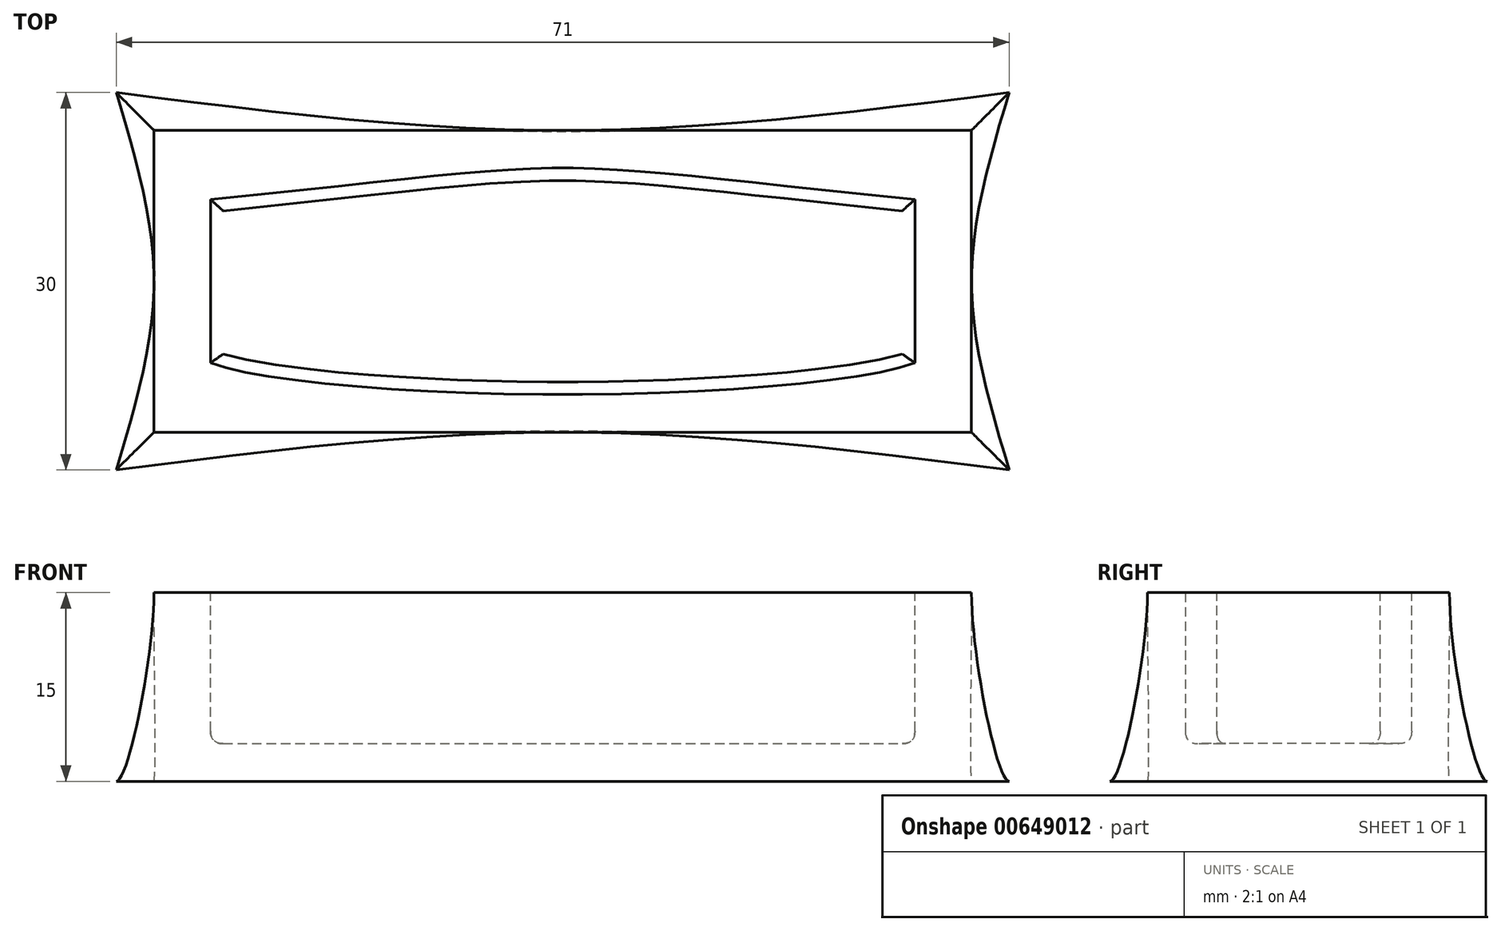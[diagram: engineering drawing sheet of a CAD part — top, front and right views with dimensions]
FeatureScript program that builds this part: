
annotation { "Feature Type Name" : "Feature", "Feature Type Description" : "" }
export const myFeature = defineFeature(function(context is Context, id is Id, definition is map)
    precondition{}
    {
        {
            var Q0;
            Q0=qCreatedBy(makeId("Top.planeOp"),FACE);
            var sketch = newSketch(context, id + "F0", { "sketchPlane" : qUnion([Q0])});
            skLineSegment(sketch, "E0", {"start": v(-35.5, 0) * mm, "end": v(35.5, 0) * mm, "construction": true});
            skLineSegment(sketch, "E1", {"start": v(-35.5, 0) * mm, "end": v(-35.5, 15) * mm, "construction": true});
            skLineSegment(sketch, "E2", {"start": v(35.5, 0) * mm, "end": v(35.5, 15) * mm, "construction": true});
            skLineSegment(sketch, "E3", {"start": v(0, 0) * mm, "end": v(0, 12) * mm, "construction": true});
            skLineSegment(sketch, "E4", {"start": v(0, 0) * mm, "end": v(-32.5, 0) * mm, "construction": true});
            skLineSegment(sketch, "E5.MirrorCS", {"start": v(-35.5, 0) * mm, "end": v(-35.5, -15) * mm, "construction": true});
            skFitSpline(sketch, "E6", {"points": [v(-35.5, 15) * mm, v(-32.5, 0) * mm, v(-35.5, -15) * mm], "startDerivative": vector(9, -30) * mm, "endDerivative": vector(-9, -30) * mm});
            skFitSpline(sketch, "E7", {"points": [v(-35.5, 15) * mm, v(0, 12) * mm, v(35.5, 15) * mm], "startDerivative": vector(71, -9) * mm, "endDerivative": vector(71, 9) * mm});
            skFitSpline(sketch, "E8.MirrorCS", {"points": [v(35.5, 15) * mm, v(32.5, 0) * mm, v(35.5, -15) * mm], "startDerivative": vector(-9, -30) * mm, "endDerivative": vector(9, -30) * mm});
            skFitSpline(sketch, "E9.MirrorCS", {"points": [v(-35.5, -15) * mm, v(0, -12) * mm, v(35.5, -15) * mm], "startDerivative": vector(71, 9) * mm, "endDerivative": vector(71, -9) * mm});
            skSolve(sketch);
        }
        {
            var Q0;
            Q0=makeQuery(id+"F0.imprint","IMPRINT",FACE,{"disambiguationData":[TD([[makeQuery(id+"F0.imprint","IMPRINT",EDGE,{"derivedFrom":sQuery(id+"F0.wireOp",EDGE,"E6")}),1.0]])]});
            cPlane(context, id + "F1", {"entities" : qUnion([Q0]), "cplaneType" : CPlaneType.OFFSET, "offset" : 15 * mm, "width" : 150 * mm, "height" : 150 * mm});
        }
        {
            var Q0;
            Q0=qCreatedBy(id+"F1.planeOp",FACE);
            var sketch = newSketch(context, id + "F2", { "sketchPlane" : qUnion([Q0])});
            skLineSegment(sketch, "E10", {"start": v(0, 0) * mm, "end": v(32.5, 0) * mm, "construction": true});
            skLineSegment(sketch, "E11", {"start": v(0, 0) * mm, "end": v(-32.5, 0) * mm, "construction": true});
            skLineSegment(sketch, "E12", {"start": v(-32.5, 0) * mm, "end": v(-32.5, 12) * mm, "construction": true});
            skLineSegment(sketch, "E13.MirrorCS", {"start": v(-32.5, 0) * mm, "end": v(-32.5, -12) * mm, "construction": true});
            skLineSegment(sketch, "E14", {"start": v(-32.5, 12) * mm, "end": v(32.5, 12) * mm});
            skLineSegment(sketch, "E15", {"start": v(32.5, 12) * mm, "end": v(32.5, -12) * mm});
            skLineSegment(sketch, "E16", {"start": v(32.5, -12) * mm, "end": v(-32.5, -12) * mm});
            skLineSegment(sketch, "E17", {"start": v(-32.5, 12) * mm, "end": v(-32.5, -12) * mm});
            skSolve(sketch);
        }
        {
            var Q0;
            Q0=makeQuery(id+"F2.imprint","IMPRINT",FACE,{"disambiguationData":[TD([[makeQuery(id+"F2.imprint","IMPRINT",EDGE,{"derivedFrom":sQuery(id+"F2.wireOp",EDGE,"E14")}),-1.0]])]});
            var Q1;
            Q1=makeQuery(id+"F0.imprint","IMPRINT",FACE,{"disambiguationData":[TD([[makeQuery(id+"F0.imprint","IMPRINT",EDGE,{"derivedFrom":sQuery(id+"F0.wireOp",EDGE,"E6")}),1.0]])]});
            loft(context, id + "F3", {"startCondition" : LoftEndDerivativeType.NORMAL_TO_PROFILE, "startMagnitude" : 1, "endCondition" : LoftEndDerivativeType.TANGENT_TO_PROFILE, "endMagnitude" : 1, "sheetProfilesArray" : [{ "sheetProfileEntities" : qUnion([Q0]) }, { "sheetProfileEntities" : qUnion([Q1]) }]});
        }
        {
            var Q0;
            Q0=makeQuery(id+"F3.opLoft","CAP_FACE",FACE,{"disambiguationData":[OSD([makeQuery(id+"F2.imprint","IMPRINT",FACE,{"disambiguationData":[TD([[makeQuery(id+"F2.imprint","IMPRINT",EDGE,{"derivedFrom":sQuery(id+"F2.wireOp",EDGE,"E14")}),-1.0]])]})])],"isStart":true});
            var sketch = newSketch(context, id + "F4", { "sketchPlane" : qUnion([Q0])});
            skLineSegment(sketch, "E18", {"start": v(0, 0) * mm, "end": v(28, 0) * mm, "construction": true});
            skLineSegment(sketch, "E19.MirrorCS", {"start": v(0, 0) * mm, "end": v(-28, 0) * mm, "construction": true});
            skLineSegment(sketch, "E20", {"start": v(0, 9) * mm, "end": v(0, -9) * mm, "construction": true});
            skLineSegment(sketch, "E21", {"start": v(-28, 6.5) * mm, "end": v(-28, -6.5) * mm});
            skLineSegment(sketch, "E22.MirrorCS", {"start": v(28, 6.5) * mm, "end": v(28, -6.5) * mm});
            skLineSegment(sketch, "E23", {"start": v(-24, -8) * mm, "end": v(24, -8) * mm, "construction": true});
            skLineSegment(sketch, "E24", {"start": v(-13, 8) * mm, "end": v(13, 8) * mm, "construction": true});
            skFitSpline(sketch, "E25", {"points": [v(-28, 6.5) * mm, v(0, 9) * mm, v(28, 6.5) * mm], "startDerivative": vector(90, 9) * mm, "endDerivative": vector(90, -9) * mm});
            skFitSpline(sketch, "E26", {"points": [v(-28, -6.5) * mm, v(0, -9) * mm, v(28, -6.5) * mm], "startDerivative": vector(24, -9) * mm, "endDerivative": vector(24, 9) * mm});
            skSolve(sketch);
        }
        {
            var Q0;
            Q0 = qSketchRegion(id + "F4", true);
            extrude(context, id + "F5", {"entities" : qUnion([Q0]), "operationType" : NewBodyOperationType.REMOVE, "oppositeDirection" : true, "depth" : 12 * mm, "offsetDistance" : 25 * mm});
        }
        {
            var Q0;
            Q0=makeQuery(id+"F5.boolean.opBoolean","COPY",FACE,{"derivedFrom":makeQuery(id+"F5.opExtrude","CAP_FACE",FACE,{"disambiguationData":[OSD([sQuery(id+"F4.wireOp",EDGE,"E21"),sQuery(id+"F4.wireOp",EDGE,"E22.MirrorCS"),sQuery(id+"F4.wireOp",EDGE,"E25"),sQuery(id+"F4.wireOp",EDGE,"E26")])],"isStart":false})});
            var Q1;
            Q1=makeQuery(id+"F5.boolean.opBoolean","COPY",EDGE,{"derivedFrom":makeQuery(id+"F5.opExtrude","CAP_EDGE",EDGE,{"disambiguationData":[OSD([sQuery(id+"F4.wireOp",EDGE,"E25")])],"isStart":true})});
            var Q2;
            Q2=makeQuery(id+"F5.boolean.opBoolean","COPY",EDGE,{"derivedFrom":makeQuery(id+"F5.opExtrude","CAP_EDGE",EDGE,{"disambiguationData":[OSD([sQuery(id+"F4.wireOp",EDGE,"E26")])],"isStart":true})});
            var Q3;
            Q3=makeQuery(id+"F5.boolean.opBoolean","COPY",EDGE,{"derivedFrom":makeQuery(id+"F5.opExtrude","CAP_EDGE",EDGE,{"disambiguationData":[OSD([sQuery(id+"F4.wireOp",EDGE,"E22.MirrorCS")])],"isStart":true})});
            var Q4;
            Q4=makeQuery(id+"F5.boolean.opBoolean","COPY",EDGE,{"derivedFrom":makeQuery(id+"F5.opExtrude","CAP_EDGE",EDGE,{"disambiguationData":[OSD([sQuery(id+"F4.wireOp",EDGE,"E21")])],"isStart":true})});
            fillet(context, id + "F6", {"entities" : qUnion([Q0, Q1, Q2, Q3, Q4]), "radius" : 1 * mm, "tangentPropagation" : true, "rho" : 0.5, "crossSection" : FilletCrossSection.CONIC, "allowEdgeOverflow" : false});
        }
    });
